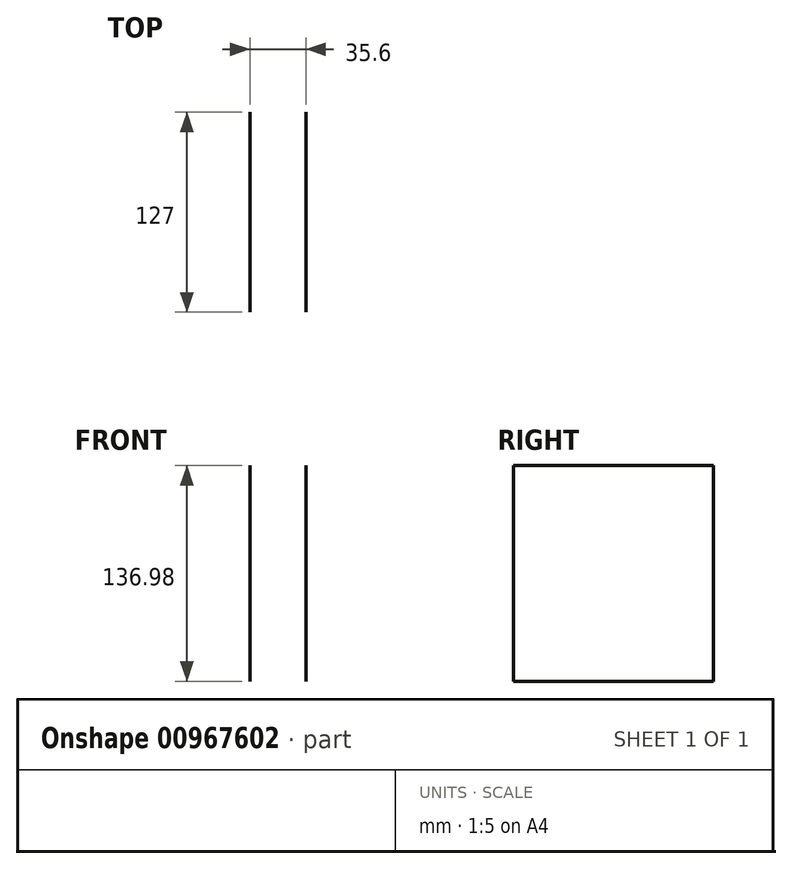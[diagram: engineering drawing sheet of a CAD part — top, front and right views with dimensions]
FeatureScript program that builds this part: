
annotation { "Feature Type Name" : "Feature", "Feature Type Description" : "" }
export const myFeature = defineFeature(function(context is Context, id is Id, definition is map)
    precondition{}
    {
        {
            var Q0;
            Q0=qCreatedBy(makeId("Front.planeOp"),FACE);
            var sketch = newSketch(context, id + "F0", { "sketchPlane" : qUnion([Q0])});
            skLineSegment(sketch, "E0.bottom", {"start": v(-17.8, -68.5) * mm, "end": v(17.8, -68.5) * mm, "construction": true});
            skLineSegment(sketch, "E0.top", {"start": v(-17.8, 68.5) * mm, "end": v(17.8, 68.5) * mm, "construction": true});
            skLineSegment(sketch, "E0.left", {"start": v(-17.8, -68.5) * mm, "end": v(-17.8, 68.5) * mm});
            skLineSegment(sketch, "E0.right", {"start": v(17.8, -68.5) * mm, "end": v(17.8, 68.5) * mm});
            skPoint(sketch, "E0.middle", {"position": v(0, 0) * mm});
            skSolve(sketch);
        }
        {
            var Q0;
            Q0=sQuery(id+"F0.wireOp",EDGE,"E0.right");
            var Q1;
            Q1=sQuery(id+"F0.wireOp",EDGE,"E0.left");
            extrude(context, id + "F1", {"bodyType" : ToolBodyType.SURFACE, "surfaceEntities" : qUnion([Q0, Q1]), "depth" : 127 * mm, "offsetDistance" : 25.4 * mm});
        }
    });
